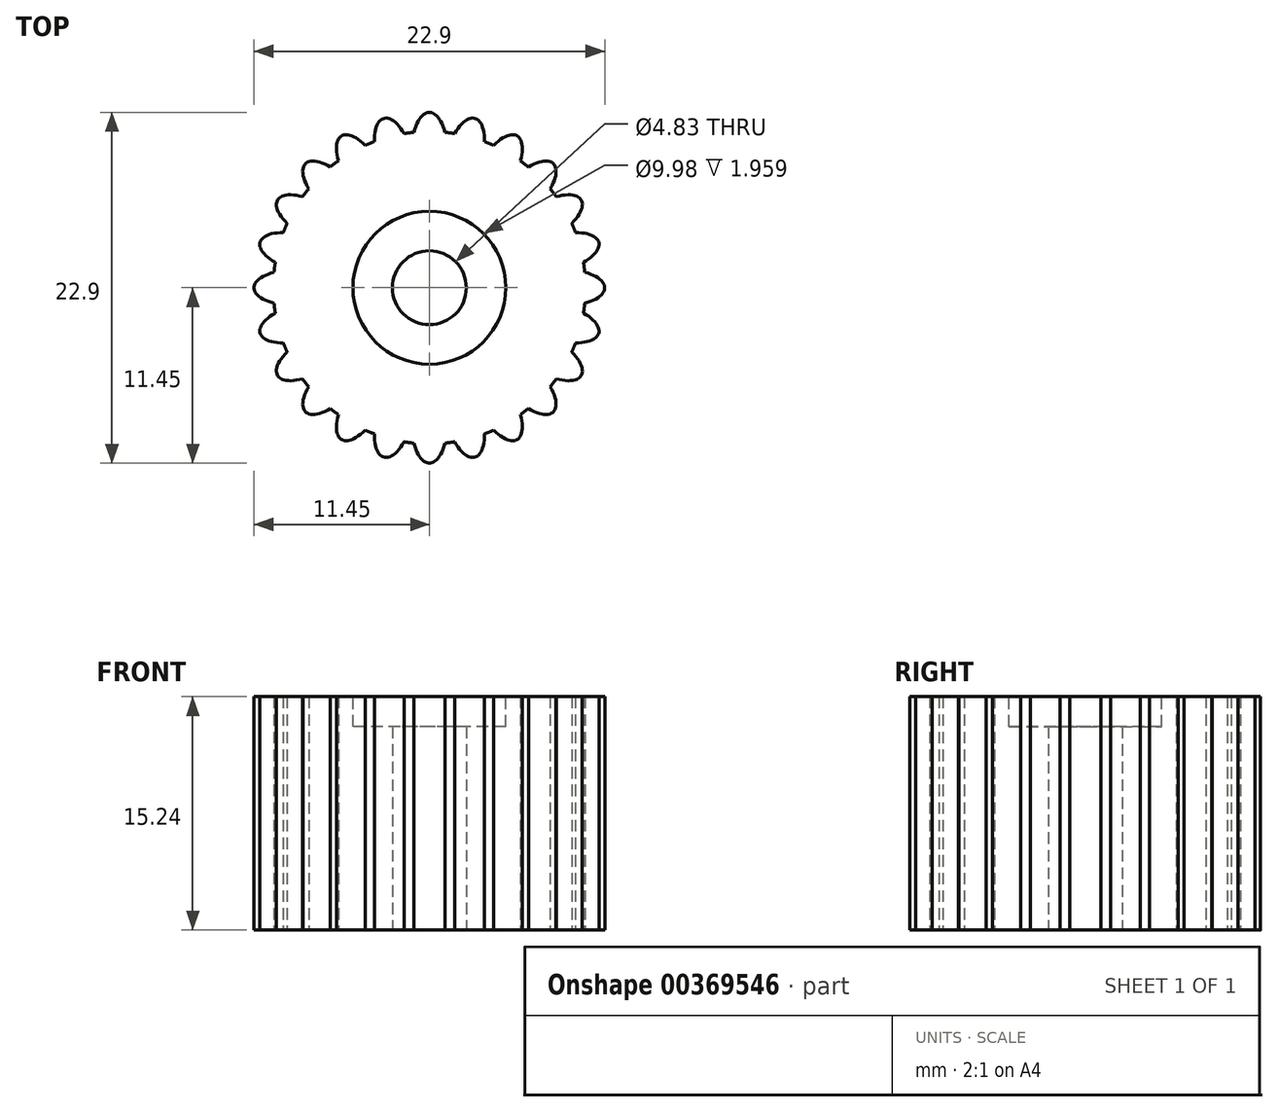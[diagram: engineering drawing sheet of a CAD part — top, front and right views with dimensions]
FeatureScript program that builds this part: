
annotation { "Feature Type Name" : "Feature", "Feature Type Description" : "" }
export const myFeature = defineFeature(function(context is Context, id is Id, definition is map)
    precondition{}
    {
        {
            var Q0;
            Q0=qCreatedBy(makeId("Top.planeOp"),FACE);
            var sketch = newSketch(context, id + "F0", { "sketchPlane" : qUnion([Q0])});
            skCircle(sketch, "E0", {"center": v(0, 0) * mm, "radius": 8.9 * mm});
            skPoint(sketch, "E1.center.orphan", {"position": v(0, 8.9) * mm});
            skEllipticalArc(sketch, "E2", {});
            skEllipticalArc(sketch, "E3.1.0", {});
            skEllipticalArc(sketch, "E3.2.0", {});
            skEllipticalArc(sketch, "E3.3.0", {});
            skEllipticalArc(sketch, "E3.4.0", {});
            skEllipticalArc(sketch, "E3.5.0", {});
            skEllipticalArc(sketch, "E3.6.0", {});
            skEllipticalArc(sketch, "E3.7.0", {});
            skEllipticalArc(sketch, "E3.8.0", {});
            skEllipticalArc(sketch, "E3.9.0", {});
            skEllipticalArc(sketch, "E3.10.0", {});
            skEllipticalArc(sketch, "E3.11.0", {});
            skEllipticalArc(sketch, "E3.12.0", {});
            skEllipticalArc(sketch, "E3.13.0", {});
            skEllipticalArc(sketch, "E3.14.0", {});
            skEllipticalArc(sketch, "E3.15.0", {});
            skEllipticalArc(sketch, "E3.16.0", {});
            skEllipticalArc(sketch, "E3.17.0", {});
            skEllipticalArc(sketch, "E3.18.0", {});
            skEllipticalArc(sketch, "E3.19.0", {});
            skEllipticalArc(sketch, "E3.20.0", {});
            skEllipticalArc(sketch, "E3.21.0", {});
            skEllipticalArc(sketch, "E3.22.0", {});
            skEllipticalArc(sketch, "E3.23.0", {});
            skCircle(sketch, "E4", {"center": v(0, 0) * mm, "radius": 10.2 * mm});
            skCircle(sketch, "E5", {"center": v(0, 0) * mm, "radius": 2.41 * mm});
            const initialGuessF0  = {"E2": [0, -0.00889, 0, -1, 0.0025605444341541723, 0.001154663274810758, 4.683000596529849, 1.6001847106497369], "E3.1.0": [0.0023009013109614096, -0.008587080595709817, 0.2588190451025207, -0.9659258262890684, 0.0025605444341541723, 0.001154663274810758, 4.683000596529849, 1.6001847106497367], "E3.2.0": [0.004445, -0.0076989658396436605, 0.5, -0.8660254037844388, 0.0025605444341541723, 0.001154663274810758, 4.683000596529849, 1.6001847106497376], "E3.3.0": [0.006286179284748408, -0.006286179284748408, 0.7071067811865478, -0.7071067811865474, 0.0025605444341541723, 0.001154663274810758, 4.6830005965298485, 1.600184710649737], "E3.4.0": [0.007698965839643658, -0.004445, 0.8660254037844387, -0.5, 0.0025605444341541723, 0.001154663274810758, 4.683000596529849, 1.600184710649736], "E3.5.0": [0.008587080595709817, -0.0023009013109614113, 0.9659258262890684, -0.2588190451025207, 0.0025605444341541723, 0.001154663274810758, 4.683000596529849, 1.6001847106497373], "E3.6.0": [0.00889, 0, 1, 0, 0.0025605444341541723, 0.001154663274810758, 4.683000596529849, 1.6001847106497369], "E3.7.0": [0.008587080595709817, 0.0023009013109614083, 0.9659258262890684, 0.2588190451025206, 0.0025605444341541723, 0.001154663274810758, 4.683000596529849, 1.6001847106497367], "E3.8.0": [0.007698965839643662, 0.004445, 0.8660254037844389, 0.5, 0.0025605444341541723, 0.001154663274810758, 4.683000596529849, 1.600184710649738], "E3.9.0": [0.006286179284748408, 0.006286179284748408, 0.7071067811865474, 0.7071067811865478, 0.0025605444341541723, 0.001154663274810758, 4.6830005965298485, 1.600184710649737], "E3.10.0": [0.004445, 0.007698965839643659, 0.5, 0.8660254037844387, 0.0025605444341541723, 0.001154663274810758, 4.6830005965298485, 1.6001847106497369], "E3.11.0": [0.0023009013109614117, 0.008587080595709817, 0.2588190451025205, 0.9659258262890684, 0.0025605444341541723, 0.001154663274810758, 4.683000596529849, 1.6001847106497373], "E3.12.0": [0, 0.00889, 0, 1, 0.0025605444341541723, 0.001154663274810758, 4.683000596529849, 1.6001847106497369], "E3.13.0": [-0.002300901310961406, 0.008587080595709819, -0.2588190451025208, 0.9659258262890684, 0.0025605444341541723, 0.001154663274810758, 4.683000596529849, 1.600184710649737], "E3.14.0": [-0.004445, 0.007698965839643661, -0.5, 0.8660254037844388, 0.0025605444341541723, 0.001154663274810758, 4.683000596529849, 1.6001847106497373], "E3.15.0": [-0.006286179284748405, 0.00628617928474841, -0.7071067811865478, 0.7071067811865472, 0.0025605444341541723, 0.001154663274810758, 4.6830005965298485, 1.6001847106497367], "E3.16.0": [-0.007698965839643658, 0.004445, -0.8660254037844388, 0.5, 0.0025605444341541723, 0.001154663274810758, 4.6830005965298485, 1.600184710649737], "E3.17.0": [-0.008587080595709815, 0.002300901310961416, -0.9659258262890684, 0.2588190451025206, 0.0025605444341541723, 0.001154663274810758, 4.683000596529849, 1.600184710649736], "E3.18.0": [-0.00889, 0, -1, 0, 0.0025605444341541723, 0.001154663274810758, 4.683000596529849, 1.6001847106497369], "E3.19.0": [-0.008587080595709819, -0.0023009013109614057, -0.9659258262890684, -0.25881904510252046, 0.0025605444341541723, 0.001154663274810758, 4.683000596529849, 1.6001847106497373], "E3.20.0": [-0.007698965839643663, -0.004445, -0.8660254037844389, -0.5, 0.0025605444341541723, 0.001154663274810758, 4.683000596529849, 1.600184710649737], "E3.21.0": [-0.006286179284748408, -0.0062861792847484065, -0.7071067811865475, -0.7071067811865476, 0.0025605444341541723, 0.001154663274810758, 4.6830005965298485, 1.6001847106497367], "E3.22.0": [-0.004445, -0.007698965839643658, -0.5, -0.8660254037844386, 0.0025605444341541723, 0.001154663274810758, 4.6830005965298485, 1.600184710649737], "E3.23.0": [-0.0023009013109614096, -0.008587080595709817, -0.2588190451025208, -0.9659258262890683, 0.0025605444341541723, 0.001154663274810758, 4.683000596529849, 1.6001847106497367]};
            skSetInitialGuess(sketch, initialGuessF0);
            skSolve(sketch);
        }
        {
            var Q0;
            Q0 = qSketchRegion(id + "F0", true);
            var Q1;
            Q1=makeQuery(id+"F0.imprint","IMPRINT",FACE,{"disambiguationData":[TD([[makeQuery(id+"F0.imprint","IMPRINT",EDGE,{"derivedFrom":sQuery(id+"F0.wireOp",EDGE,"E5")}),-1.0]])]});
            extrude(context, id + "F1", {"entities" : qUnion([Q0, Q1]), "endBound" : BoundingType.SYMMETRIC, "depth" : 15.24 * mm});
        }
        {
            var Q0;
            Q0=makeQuery(id+"F1.opExtrude","CAP_FACE",FACE,{"disambiguationData":[OSD([sQuery(id+"F0.wireOp",EDGE,"E2"),sQuery(id+"F0.wireOp",EDGE,"E3.1.0"),sQuery(id+"F0.wireOp",EDGE,"E3.2.0"),sQuery(id+"F0.wireOp",EDGE,"E3.3.0"),sQuery(id+"F0.wireOp",EDGE,"E3.4.0"),sQuery(id+"F0.wireOp",EDGE,"E3.5.0"),sQuery(id+"F0.wireOp",EDGE,"E3.6.0"),sQuery(id+"F0.wireOp",EDGE,"E3.7.0"),sQuery(id+"F0.wireOp",EDGE,"E3.8.0"),sQuery(id+"F0.wireOp",EDGE,"E3.9.0"),sQuery(id+"F0.wireOp",EDGE,"E3.10.0"),sQuery(id+"F0.wireOp",EDGE,"E3.11.0"),sQuery(id+"F0.wireOp",EDGE,"E3.12.0"),sQuery(id+"F0.wireOp",EDGE,"E3.13.0"),sQuery(id+"F0.wireOp",EDGE,"E3.14.0"),sQuery(id+"F0.wireOp",EDGE,"E3.15.0"),sQuery(id+"F0.wireOp",EDGE,"E3.16.0"),sQuery(id+"F0.wireOp",EDGE,"E3.17.0"),sQuery(id+"F0.wireOp",EDGE,"E3.18.0"),sQuery(id+"F0.wireOp",EDGE,"E3.19.0"),sQuery(id+"F0.wireOp",EDGE,"E3.20.0"),sQuery(id+"F0.wireOp",EDGE,"E3.21.0"),sQuery(id+"F0.wireOp",EDGE,"E3.22.0"),sQuery(id+"F0.wireOp",EDGE,"E3.23.0"),sQuery(id+"F0.wireOp",EDGE,"E4"),sQuery(id+"F0.wireOp",EDGE,"E5")])],"isStart":false});
            var sketch = newSketch(context, id + "F2", { "sketchPlane" : qUnion([Q0])});
            skCircle(sketch, "E6", {"center": v(0, 0) * mm, "radius": 5 * mm});
            skSolve(sketch);
        }
        {
            var Q0;
            Q0=makeQuery(id+"F2.imprint","IMPRINT",FACE,{"disambiguationData":[TD([[makeQuery(id+"F2.imprint","IMPRINT",EDGE,{"derivedFrom":sQuery(id+"F2.wireOp",EDGE,"E6")}),1.0]])]});
            extrude(context, id + "F3", {"entities" : qUnion([Q0]), "operationType" : NewBodyOperationType.REMOVE, "oppositeDirection" : true, "depth" : 1.96 * mm});
        }
    });
